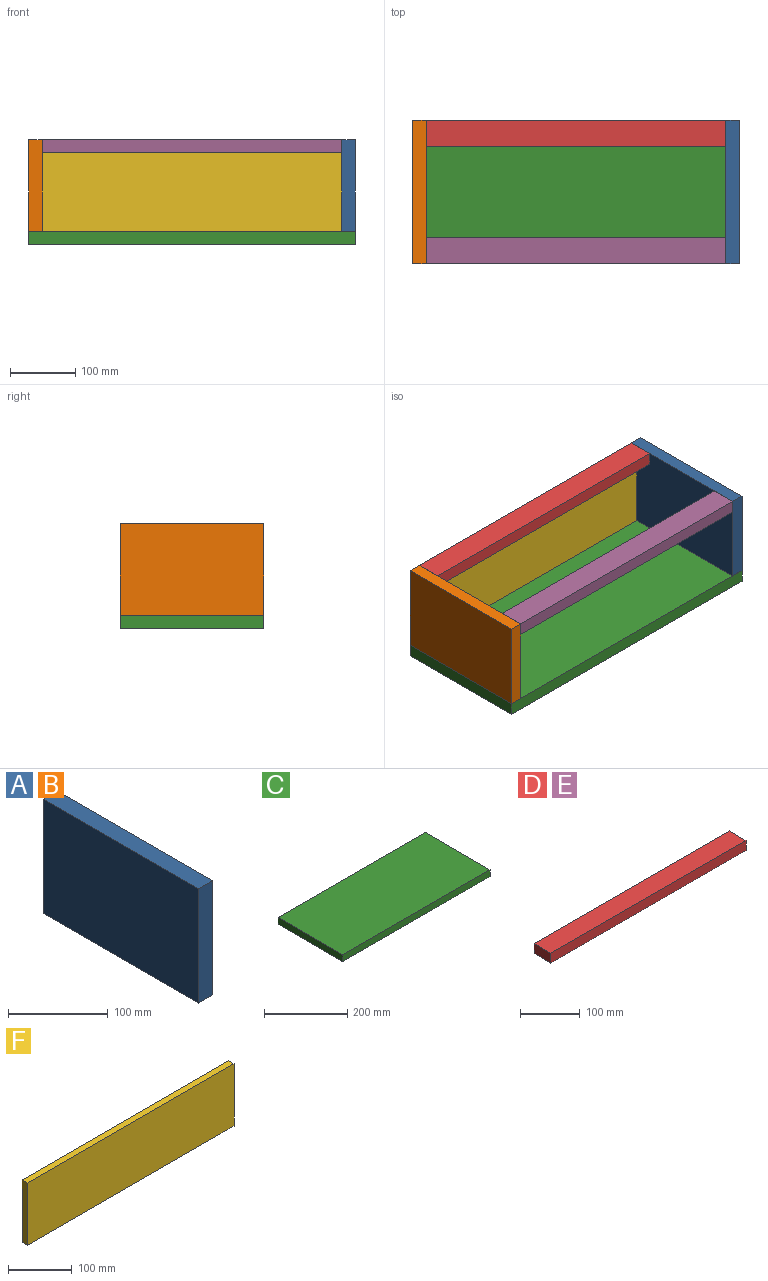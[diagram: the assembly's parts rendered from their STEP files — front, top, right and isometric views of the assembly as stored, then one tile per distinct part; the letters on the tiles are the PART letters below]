
ASSEMBLY  parts=6 mates=5
PART A: 6 faces, bbox 20x220x140 mm
  f0: plane 220x20mm, normal (0,0,1), area 4400mm2, adj f1,f3,f4,f5
  f1: plane 140x20mm, normal (0,-1,0), area 2800mm2, adj f0,f2,f4,f5
  f2: plane 220x20mm, normal (0,0,-1), area 4400mm2, adj f1,f3,f4,f5
  f3: plane 140x20mm, normal (0,1,0), area 2800mm2, adj f0,f2,f4,f5
  f4: plane 220x140mm, normal (1,0,0), area 30800mm2, adj f0,f1,f2,f3
  f5: plane 220x140mm, normal (-1,0,0), area 30800mm2, adj f0,f1,f2,f3
PART B: same geometry as A
PART C: 6 faces, bbox 500x220x20 mm
  f0: plane 500x20mm, normal (0,-1,0), area 10000mm2, adj f1,f3,f4,f5
  f1: plane 220x20mm, normal (1,0,0), area 4400mm2, adj f0,f2,f4,f5
  f2: plane 500x20mm, normal (0,1,0), area 10000mm2, adj f1,f3,f4,f5
  f3: plane 220x20mm, normal (-1,0,0), area 4400mm2, adj f0,f2,f4,f5
  f4: plane 500x220mm, normal (0,0,1), area 110000mm2, adj f0,f1,f2,f3
  f5: plane 500x220mm, normal (0,0,-1), area 110000mm2, adj f0,f1,f2,f3
PART D: 6 faces, bbox 460x40x20 mm
  f0: plane 460x20mm, normal (0,-1,0), area 9200mm2, adj f1,f3,f4,f5
  f1: plane 40x20mm, normal (1,0,0), area 800mm2, adj f0,f2,f4,f5
  f2: plane 460x20mm, normal (0,1,0), area 9200mm2, adj f1,f3,f4,f5
  f3: plane 40x20mm, normal (-1,0,0), area 800mm2, adj f0,f2,f4,f5
  f4: plane 460x40mm, normal (0,0,1), area 18400mm2, adj f0,f1,f2,f3
  f5: plane 460x40mm, normal (0,0,-1), area 18400mm2, adj f0,f1,f2,f3
PART E: same geometry as D
PART F: 6 faces, bbox 460x12x120 mm
  f0: plane 460x12mm, normal (0,0,-1), area 5520mm2, adj f1,f3,f4,f5
  f1: plane 120x12mm, normal (1,0,0), area 1440mm2, adj f0,f2,f4,f5
  f2: plane 460x12mm, normal (0,0,1), area 5520mm2, adj f1,f3,f4,f5
  f3: plane 120x12mm, normal (-1,0,0), area 1440mm2, adj f0,f2,f4,f5
  f4: plane 460x120mm, normal (0,-1,0), area 55200mm2, adj f0,f1,f2,f3
  f5: plane 460x120mm, normal (0,1,0), area 55200mm2, adj f0,f1,f2,f3
PLACE A t=(207.64,-24.47,52.67)mm
PLACE B t=(-272.36,-24.47,52.67)mm
PLACE C t=(-22.36,-24.47,-37.33)mm
PLACE D t=(-22.36,65.53,102.67)mm
PLACE E t=(-22.36,-114.47,102.67)mm
PLACE F t=(-14.24,85.53,42.67)mm
MATE fastened F.f0 <-> B.f2  axis (0,0,-1) through (-252.36,85.53,-17.33)mm
MATE fastened A.f2 <-> C.f4  axis (0,0,-1) through (227.64,-134.47,-17.33)mm
MATE fastened D.f3 <-> B.f4  axis (-1,0,0) through (-252.36,85.53,122.67)mm
MATE fastened B.f2 <-> C.f4  axis (0,0,-1) through (-272.36,-134.47,-17.33)mm
MATE fastened E.f3 <-> B.f4  axis (-1,0,0) through (-252.36,-134.47,122.67)mm
